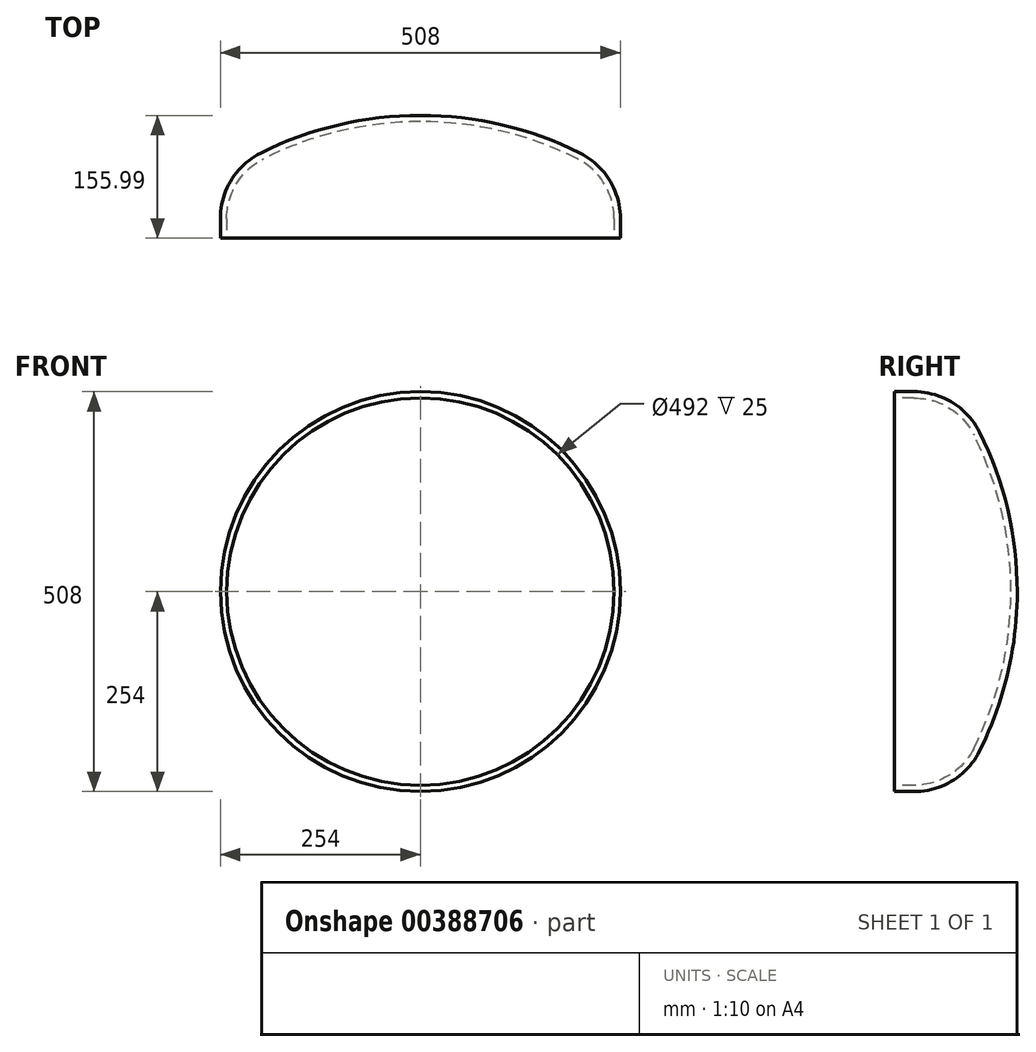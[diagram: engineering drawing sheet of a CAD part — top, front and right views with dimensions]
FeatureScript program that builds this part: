
annotation { "Feature Type Name" : "Feature", "Feature Type Description" : "" }
export const myFeature = defineFeature(function(context is Context, id is Id, definition is map)
    precondition{}
    {
        {
            var Q0;
            Q0=qCreatedBy(makeId("Right.planeOp"),FACE);
            var sketch = newSketch(context, id + "F0", { "sketchPlane" : qUnion([Q0])});
            skLineSegment(sketch, "E0", {"start": v(0, 0) * mm, "end": v(147.99, 0) * mm, "construction": true});
            skLineSegment(sketch, "E1", {"start": v(0, 246) * mm, "end": v(25, 246) * mm});
            skArc(sketch, "E2", {"start": v(25, 246) * mm, "mid": v(69.67, 233.31) * mm, "end": v(101, 199.03) * mm});
            skArc(sketch, "E3", {"start": v(101, 199.03) * mm, "mid": v(136.08, 102.25) * mm, "end": v(147.99, 0) * mm});
            skArc(sketch, "E4.0", {"start": v(108.15, 202.61) * mm, "mid": v(143.87, 104.1) * mm, "end": v(155.99, 0) * mm});
            skArc(sketch, "E4.1", {"start": v(25, 254) * mm, "mid": v(73.88, 240.12) * mm, "end": v(108.15, 202.61) * mm});
            skLineSegment(sketch, "E4.2", {"start": v(0, 254) * mm, "end": v(25, 254) * mm});
            skLineSegment(sketch, "E5", {"start": v(0, 254) * mm, "end": v(0, 246) * mm});
            skLineSegment(sketch, "E6", {"start": v(147.99, 0) * mm, "end": v(155.99, 0) * mm});
            skSolve(sketch);
        }
        {
            var Q0;
            Q0 = qSketchRegion(id + "F0", true);
            var Q1;
            Q1=sQuery(id+"F0.wireOp",EDGE,"E0");
            revolve(context, id + "F1", {"entities" : qUnion([Q0]), "axis" : qUnion([Q1]), "revolveType" : RevolveType.FULL});
        }
    });
